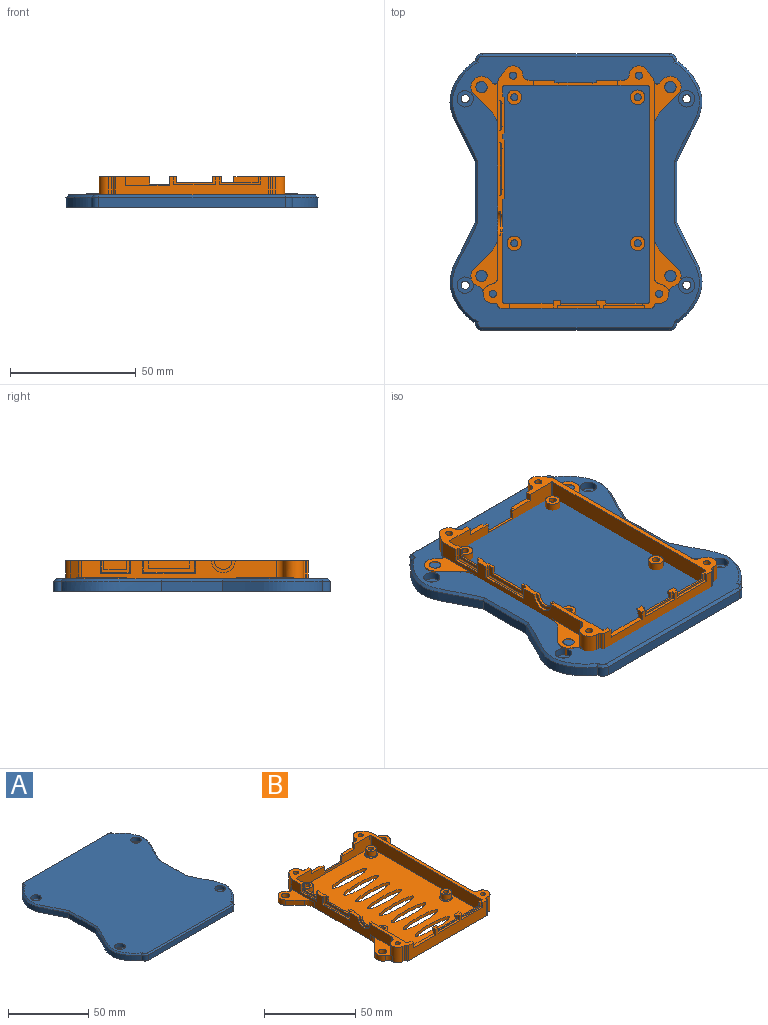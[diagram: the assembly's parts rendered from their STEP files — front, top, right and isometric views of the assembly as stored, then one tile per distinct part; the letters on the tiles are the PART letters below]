
ASSEMBLY  parts=2 mates=1
PART A: 43 faces, bbox 102.5x111.1x6.1 mm
  f0: plane 70.5x2mm, normal (0,1,0), area 141mm2, adj f1,f15,f16,f30
  f1: plane 102x2mm, normal (1,0,0), area 204mm2, adj f0,f2,f16,f30
  f2: plane 70.5x2mm, normal (0,-1,0), area 141mm2, adj f1,f15,f16,f30
  f3: extruded ~40x10.04mm, area 183.4mm2, adj f4,f14,f16,f41
  f4: plane 24x4mm, normal (-1,0,0), area 96mm2, adj f3,f5,f16,f39
  f5: extruded ~40x10.04mm, area 183.4mm2, adj f4,f6,f16,f37
  f6: cylinder r=3mm len=4mm, axis (0,0,1), area 18.8mm2, adj f5,f7,f16,f35
  f7: plane 74x4mm, normal (0,-1,0), area 296mm2, adj f6,f8,f16,f33
  f8: cylinder r=3mm len=4mm, axis (0,0,1), area 18.8mm2, adj f7,f9,f16,f31
  f9: extruded ~40x10.04mm, area 183.4mm2, adj f8,f10,f16,f32
  f10: plane 24x4mm, normal (1,0,0), area 96mm2, adj f9,f11,f16,f34
  f11: extruded ~40x10.04mm, area 183.4mm2, adj f10,f12,f16,f36
  f12: cylinder r=3mm len=4mm, axis (0,0,1), area 18.8mm2, adj f11,f13,f16,f38
  f13: plane 74x4mm, normal (0,1,0), area 296mm2, adj f12,f14,f16,f40
  f14: cylinder r=3mm len=4mm, axis (0,0,1), area 18.8mm2, adj f3,f13,f16,f42
  f15: plane 102x2mm, normal (-1,0,0), area 204mm2, adj f0,f2,f16,f30
  f16: plane 110x101.38mm, normal (0,0,-1), area 2552.6mm2, adj f0,f1,f2,f3,f4,f5,f6,f7
  f17: plane 109.12x99.61mm, normal (0,0,1), area 9261.1mm2, adj f20,f23,f26,f29,f31,f32,f33,f34
  f18: cylinder r=1.65mm len=3.3mm, axis (0,0,1), area 20.7mm2, adj f16,f19
  f19: plane 6.5x6.5mm, normal (0,0,1), area 24.6mm2, adj f18,f20
  f20: cylinder r=3.25mm len=6.5mm, axis (0,0,1), area 61.3mm2, adj f17,f19
  f21: cylinder r=1.65mm len=3.3mm, axis (0,0,1), area 20.7mm2, adj f16,f22
  f22: plane 6.5x6.5mm, normal (0,0,1), area 24.6mm2, adj f21,f23
  f23: cylinder r=3.25mm len=6.5mm, axis (0,0,1), area 61.3mm2, adj f17,f22
  f24: cylinder r=1.65mm len=3.3mm, axis (0,0,1), area 20.7mm2, adj f16,f25
  f25: plane 6.5x6.5mm, normal (0,0,1), area 24.6mm2, adj f24,f26
  f26: cylinder r=3.25mm len=6.5mm, axis (0,0,1), area 61.3mm2, adj f17,f25
  f27: cylinder r=1.65mm len=3.3mm, axis (0,0,1), area 20.7mm2, adj f16,f28
  f28: plane 6.5x6.5mm, normal (0,0,1), area 24.6mm2, adj f27,f29
  f29: cylinder r=3.25mm len=6.5mm, axis (0,0,1), area 61.3mm2, adj f17,f28
  f30: plane 102x70.5mm, normal (0,0,-1), area 7191mm2, adj f0,f1,f2,f15
  f31: cone r=2mm half-angle=45deg, axis (0,0,-1), area 6mm2, adj f8,f17,f32,f33
  f32: bspline ~40.52x11.13mm, area 64.4mm2, adj f9,f17,f31,f34
  f33: plane 74x1mm, normal (0,-0.71,0.71), area 104.7mm2, adj f7,f17,f31,f35
  f34: plane 24.39x1mm, normal (0.71,0,0.71), area 34.2mm2, adj f10,f17,f32,f36
  f35: cone r=2mm half-angle=45deg, axis (0,0,-1), area 6mm2, adj f6,f17,f33,f37
  f36: bspline ~43.19x12.21mm, area 64.4mm2, adj f11,f17,f34,f38
  f37: bspline ~43.19x12.21mm, area 64.4mm2, adj f5,f17,f35,f39
  f38: cone r=2mm half-angle=45deg, axis (0,0,-1), area 6mm2, adj f12,f17,f36,f40
  f39: plane 24.39x1mm, normal (-0.71,0,0.71), area 34.2mm2, adj f4,f17,f37,f41
  f40: plane 74x1mm, normal (0,0.71,0.71), area 104.7mm2, adj f13,f17,f38,f42
  f41: bspline ~40.52x11.13mm, area 64.4mm2, adj f3,f17,f39,f42
  f42: cone r=2mm half-angle=45deg, axis (0,0,-1), area 6mm2, adj f14,f17,f40,f41
PART B: 166 faces, bbox 83.8x96.6x10.6 mm
  f0: plane 96.58x83.83mm, normal (0,0,-1), area 5354.5mm2, adj f1,f6,f7,f8,f9,f37,f38,f39
  f1: cylinder r=2.25mm len=4.5mm, axis (0,0,-1), area 49.5mm2, adj f0,f3
  f2: plane 22.79x10.75mm, normal (0,0,1), area 100.2mm2, adj f8,f9,f89,f119,f120,f121,f122,f123
  f3: plane 22.79x10.75mm, normal (0,0,1), area 100.2mm2, adj f1,f39,f148,f149,f150,f151,f152,f153
  f4: plane 20.07x10.76mm, normal (0,0,1), area 93.7mm2, adj f6,f39,f41,f143,f144,f145,f146,f147
  f5: plane 20.07x10.76mm, normal (0,0,1), area 93.7mm2, adj f7,f89,f124,f125,f126,f127,f128,f129
  f6: cylinder r=2.25mm len=4.5mm, axis (0,0,-1), area 49.5mm2, adj f0,f4
  f7: cylinder r=2.25mm len=4.5mm, axis (0,0,-1), area 49.5mm2, adj f0,f5
  f8: cylinder r=2.25mm len=4.5mm, axis (0,0,-1), area 49.5mm2, adj f0,f2
  f9: cylinder r=3.9mm len=10.3mm, axis (0,0,-1), area 101.4mm2, adj f0,f2,f12,f119,f123,f135
  f10: plane 3x2.8mm, normal (0,0,1), area 7.2mm2, adj f25,f28,f30,f37,f158,f159
  f11: plane 3.5x3mm, normal (0,0,1), area 8.1mm2, adj f29,f32,f35,f37,f159,f160,f163,f165
  f12: plane 30.25x10.45mm, normal (0,0,1), area 99.5mm2, adj f9,f22,f26,f37,f84,f85,f86,f87
  f13: plane 8.65x2.5mm, normal (0,0,1), area 15.1mm2, adj f85,f89,f91,f92,f93,f94,f96,f97
  f14: plane 9.75x2.5mm, normal (0,0,1), area 16.8mm2, adj f85,f86,f87,f88,f89,f94,f97,f103
  f15: plane 15.1x14.15mm, normal (0,0,1), area 78mm2, adj f17,f45,f50,f85,f89,f93,f95,f96
  f16: plane 96.25x20.25mm, normal (0,0,1), area 280.9mm2, adj f23,f24,f26,f34,f35,f36,f37,f38
  f17: cylinder r=1.4mm len=8.3mm, axis (0,0,-1), area 73mm2, adj f15,f20
  f18: plane 2.8x2.8mm, normal (0,0,1), area 6.2mm2, adj f22
  f19: plane 2.8x2.8mm, normal (0,0,1), area 6.2mm2, adj f23
  f20: plane 2.8x2.8mm, normal (0,0,1), area 6.2mm2, adj f17
  f21: plane 2.8x2.8mm, normal (0,0,1), area 6.2mm2, adj f24
  f22: cylinder r=1.4mm len=8.3mm, axis (0,0,-1), area 73mm2, adj f12,f18
  f23: cylinder r=1.4mm len=8.3mm, axis (0,0,1), area 73mm2, adj f16,f19
  f24: cylinder r=1.4mm len=8.3mm, axis (0,0,-1), area 73mm2, adj f16,f21
  f25: plane 3.6x3mm, normal (-1,0,0), area 8.7mm2, adj f10,f26,f27,f30,f37,f157
  f26: plane 57x8.3mm, normal (0,1,0), area 322.8mm2, adj f12,f16,f25,f27,f28,f31,f32,f33
  f27: plane 2.8x2mm, normal (0,0.89,-0.45), area 6.3mm2, adj f25,f26,f28,f30
  f28: plane 2.55x1.8mm, normal (1,0,0), area 3.5mm2, adj f10,f26,f27,f30,f159,f164
  f29: plane 3.5x0.55mm, normal (0,1,0), area 1.9mm2, adj f11,f31,f32,f165
  f30: plane 2.8x0.55mm, normal (0,1,0), area 1.5mm2, adj f10,f25,f27,f28
  f31: plane 3.5x2mm, normal (0,0.89,-0.45), area 7.8mm2, adj f26,f29,f32,f165
  f32: plane 2.55x1.8mm, normal (1,0,0), area 3.5mm2, adj f11,f26,f29,f31,f33,f35
  f33: plane 14.5x0.8mm, normal (0,0,1), area 11.6mm2, adj f26,f32,f34,f35
  f34: plane 2.47x0.8mm, normal (-1,0,0), area 2mm2, adj f16,f26,f33,f35
  f35: plane 16.5x3.17mm, normal (0,-1,0), area 16.5mm2, adj f11,f16,f32,f33,f34,f36,f162,f163
  f36: plane 3.17x1.2mm, normal (-1,0,0), area 3.8mm2, adj f16,f35,f37,f162
  f37: plane 60.4x10.3mm, normal (0,-1,0), area 454.9mm2, adj f0,f10,f11,f12,f16,f25,f36,f38
  f38: cylinder r=0.8mm len=10.3mm, axis (0,0,-1), area 12.9mm2, adj f0,f16,f37,f40
  f39: plane 77.46x10.3mm, normal (1,0,0), area 678.5mm2, adj f0,f3,f4,f16,f41,f147,f148,f153
  f40: plane 10.3x0.18mm, normal (1,0,0), area 1.9mm2, adj f0,f16,f38,f155
  f41: cylinder r=2mm len=10.3mm, axis (0,0,1), area 12.1mm2, adj f0,f4,f16,f39,f42,f143
  f42: plane 10.3x3.48mm, normal (0.82,0.58,0), area 43.8mm2, adj f0,f16,f41,f43
  f43: cylinder r=3.9mm len=10.3mm, axis (0,0,-1), area 99.9mm2, adj f0,f16,f42,f44
  f44: cylinder r=2mm len=10.3mm, axis (0,0,1), area 31.5mm2, adj f0,f16,f43,f45
  f45: plane 38.21x10.3mm, normal (0,1,0), area 205.6mm2, adj f0,f15,f16,f44,f46,f47,f51,f132
  f46: plane 5.3x1mm, normal (-1,0,0), area 5.3mm2, adj f45,f47,f48,f142
  f47: plane 10x2mm, normal (0,0,1), area 18.5mm2, adj f45,f46,f48,f49,f50,f51
  f48: plane 16.5x5.3mm, normal (0,1,0), area 36.1mm2, adj f46,f47,f49,f138,f139,f140,f141,f142
  f49: plane 3.8x1mm, normal (-1,0,0), area 3.8mm2, adj f47,f48,f50,f140
  f50: plane 57x8.3mm, normal (0,-1,0), area 321.3mm2, adj f15,f16,f47,f49,f51,f52,f55,f136
  f51: plane 3x2mm, normal (-1,0,0), area 6mm2, adj f16,f45,f47,f50
  f52: cylinder r=0.5mm len=8.3mm, axis (0,0,1), area 6.5mm2, adj f16,f50,f53,f55
  f53: plane 85.6x8.3mm, normal (-1,0,0), area 710.5mm2, adj f16,f52,f54,f55
  f54: cylinder r=0.5mm len=8.3mm, axis (0,0,1), area 6.5mm2, adj f16,f26,f53,f55
  f55: plane 86.93x58.33mm, normal (0,0,1), area 4061mm2, adj f26,f50,f52,f53,f54,f56,f57,f58
  f56: extruded ~26x5mm, area 109.1mm2, adj f0,f55
  f57: extruded ~26x5mm, area 109.1mm2, adj f0,f55
  f58: extruded ~26x5mm, area 109.1mm2, adj f0,f55
  f59: extruded ~26x5mm, area 109.1mm2, adj f0,f55
  f60: extruded ~26x5mm, area 109.1mm2, adj f0,f55
  f61: extruded ~26x5mm, area 109.1mm2, adj f0,f55
  f62: extruded ~26x5mm, area 109.1mm2, adj f0,f55
  f63: extruded ~26x5mm, area 109.1mm2, adj f0,f55
  f64: cone r=3.15mm half-angle=45deg, axis (0,0,-1), area 14mm2, adj f55,f65
  f65: cylinder r=2.9mm len=5.8mm, axis (0,0,1), area 63.8mm2, adj f64,f67
  f66: plane 5.8x5.8mm, normal (0,0,1), area 20.3mm2, adj f70,f72
  f67: plane 5.8x5.8mm, normal (0,0,1), area 20.3mm2, adj f65,f77
  f68: plane 5.8x5.8mm, normal (0,0,1), area 20.3mm2, adj f79,f80
  f69: plane 5.8x5.8mm, normal (0,0,1), area 20.3mm2, adj f78,f82
  f70: cylinder r=2.9mm len=5.8mm, axis (0,0,1), area 63.8mm2, adj f66,f71
  f71: cone r=3.15mm half-angle=45deg, axis (0,0,-1), area 14mm2, adj f55,f70
  f72: cylinder r=1.4mm len=5mm, axis (0,0,1), area 44mm2, adj f66,f75
  f73: plane 2.8x2.8mm, normal (0,0,1), area 6.2mm2, adj f77
  f74: plane 2.8x2.8mm, normal (0,0,1), area 6.2mm2, adj f78
  f75: plane 2.8x2.8mm, normal (0,0,1), area 6.2mm2, adj f72
  f76: plane 2.8x2.8mm, normal (0,0,1), area 6.2mm2, adj f79
  f77: cylinder r=1.4mm len=5mm, axis (0,0,1), area 44mm2, adj f67,f73
  f78: cylinder r=1.4mm len=5mm, axis (0,0,1), area 44mm2, adj f69,f74
  f79: cylinder r=1.4mm len=5mm, axis (0,0,1), area 44mm2, adj f68,f76
  f80: cylinder r=2.9mm len=5.8mm, axis (0,0,1), area 63.8mm2, adj f68,f81
  f81: cone r=3.15mm half-angle=45deg, axis (0,0,-1), area 14mm2, adj f55,f80
  f82: cylinder r=2.9mm len=5.8mm, axis (0,0,1), area 63.8mm2, adj f69,f83
  f83: cone r=3.15mm half-angle=45deg, axis (0,0,-1), area 14mm2, adj f55,f82
  f84: cylinder r=0.5mm len=8.3mm, axis (0,0,-1), area 6.5mm2, adj f12,f26,f55,f85
  f85: plane 85.6x8.3mm, normal (1,0,0), area 494.1mm2, adj f12,f13,f14,f15,f55,f84,f86,f98
  f86: cylinder r=3.5mm len=7mm, axis (-1,0,0), area 11mm2, adj f12,f14,f85,f87
  f87: plane 9.5x4.75mm, normal (-1,0,0), area 16.2mm2, adj f12,f14,f86,f88
  f88: cylinder r=4.75mm len=9.5mm, axis (-1,0,0), area 14.9mm2, adj f12,f14,f87,f89
  f89: plane 77.46x10.3mm, normal (-1,0,0), area 472.5mm2, adj f0,f2,f5,f12,f13,f14,f15,f88
  f90: plane 10.3x0.18mm, normal (-1,0,0), area 1.9mm2, adj f0,f12,f133,f134
  f91: plane 5.12x1mm, normal (0,-1,0), area 5.1mm2, adj f13,f89,f92,f117
  f92: plane 5.12x0.5mm, normal (-0.71,-0.71,0), area 3.4mm2, adj f13,f91,f94,f118
  f93: plane 11x4.75mm, normal (-1,0,0), area 18.5mm2, adj f13,f15,f95,f101,f102,f109,f112,f113
  f94: plane 20x4.62mm, normal (-1,0,0), area 40.9mm2, adj f13,f14,f92,f103,f104,f105,f115,f118
  f95: plane 3.75x1mm, normal (0,-1,0), area 3.8mm2, adj f15,f93,f96,f102
  f96: plane 14x5.25mm, normal (1,0,0), area 39.8mm2, adj f13,f15,f95,f98,f99,f100,f101,f102
  f97: plane 23x3.62mm, normal (1,0,0), area 31.8mm2, adj f13,f14,f103,f104,f105,f106,f107,f108
  f98: plane 5.75x0.5mm, normal (0.71,0.71,0), area 3.9mm2, adj f15,f85,f96,f99
  f99: plane 15x0.5mm, normal (0.71,0,-0.71), area 10.3mm2, adj f85,f96,f98,f100
  f100: plane 5.75x0.5mm, normal (0.71,-0.71,0), area 3.9mm2, adj f13,f85,f96,f99
  f101: plane 3.75x1mm, normal (0,1,0), area 3.8mm2, adj f13,f93,f96,f102
  f102: plane 9x1mm, normal (0,0,1), area 9mm2, adj f93,f95,f96,f101
  f103: plane 3.12x1mm, normal (0,1,0), area 3.1mm2, adj f14,f94,f97,f104
  f104: plane 16.5x1mm, normal (0,0,1), area 16.5mm2, adj f94,f97,f103,f105
  f105: plane 3.12x1mm, normal (0,-1,0), area 3.1mm2, adj f13,f94,f97,f104
  f106: plane 4.62x0.5mm, normal (0.71,0.71,0), area 2.9mm2, adj f13,f85,f97,f107
  f107: plane 24x1mm, normal (0.89,0,-0.45), area 26.3mm2, adj f85,f97,f106,f108
  f108: plane 4.62x0.5mm, normal (0.71,-0.71,0), area 2.9mm2, adj f14,f85,f97,f107
  f109: plane 5.25x0.5mm, normal (-0.71,0.71,0), area 3.5mm2, adj f13,f93,f110,f112
  f110: plane 5.25x1mm, normal (0,1,0), area 5.2mm2, adj f13,f89,f109,f111
  f111: plane 12x1mm, normal (0,0,1), area 12mm2, adj f89,f110,f112,f114
  f112: plane 12x0.5mm, normal (-0.71,0,0.71), area 8.1mm2, adj f93,f109,f111,f113
  f113: plane 5.25x0.5mm, normal (-0.71,-0.71,0), area 3.5mm2, adj f15,f93,f112,f114
  f114: plane 5.25x1mm, normal (0,-1,0), area 5.2mm2, adj f15,f89,f111,f113
  f115: plane 5.12x0.5mm, normal (-0.71,0.71,0), area 3.4mm2, adj f14,f94,f116,f118
  f116: plane 5.12x1mm, normal (0,1,0), area 5.1mm2, adj f14,f89,f115,f117
  f117: plane 21x1mm, normal (0,0,1), area 21mm2, adj f89,f91,f116,f118
  f118: plane 21x0.5mm, normal (-0.71,0,0.71), area 14.5mm2, adj f92,f94,f115,f117
  f119: cylinder r=3mm len=6.8mm, axis (0,0,-1), area 29.1mm2, adj f2,f9,f12,f89
  f120: cylinder r=8mm len=5.66mm, axis (0,0,-1), area 22mm2, adj f0,f2,f89,f121
  f121: plane 7.16x7.16mm, normal (-0.71,0.71,0), area 35.5mm2, adj f0,f2,f120,f122
  f122: cylinder r=4.25mm len=7.02mm, axis (0,0,-1), area 30mm2, adj f0,f2,f121,f123
  f123: cylinder r=3mm len=3.5mm, axis (0,0,-1), area 13.4mm2, adj f0,f2,f9,f122
  f124: cylinder r=8mm len=5.66mm, axis (0,0,1), area 22mm2, adj f0,f5,f89,f125
  f125: plane 7.16x7.16mm, normal (-0.71,-0.71,0), area 35.5mm2, adj f0,f5,f124,f126
  f126: cylinder r=4.25mm len=7.26mm, axis (0,0,-1), area 46.7mm2, adj f0,f5,f125,f127
  f127: plane 3.5x1.45mm, normal (0.71,0.71,0), area 7.2mm2, adj f0,f5,f126,f128
  f128: cylinder r=1.2mm len=3.5mm, axis (0,0,-1), area 9.6mm2, adj f0,f5,f127,f129
  f129: cylinder r=2mm len=10.3mm, axis (0,0,-1), area 12.1mm2, adj f0,f5,f15,f89,f128,f130
  f130: plane 10.3x3.48mm, normal (-0.82,0.58,0), area 43.8mm2, adj f0,f15,f129,f131
  f131: cylinder r=3.9mm len=10.3mm, axis (0,0,-1), area 99.9mm2, adj f0,f15,f130,f132
  f132: cylinder r=2mm len=10.3mm, axis (0,0,-1), area 31.5mm2, adj f0,f15,f45,f131
  f133: cylinder r=0.8mm len=10.3mm, axis (0,0,1), area 12.9mm2, adj f0,f12,f37,f90
  f134: cylinder r=0.8mm len=10.3mm, axis (0,0,1), area 12.9mm2, adj f0,f12,f90,f135
  f135: plane 10.3x1.2mm, normal (0,-1,0), area 12.4mm2, adj f0,f9,f12,f134
  f136: cylinder r=0.5mm len=8.3mm, axis (0,0,1), area 6.5mm2, adj f15,f50,f55,f85
  f137: plane 3x2mm, normal (1,0,0), area 6mm2, adj f15,f45,f50,f138
  f138: plane 10x2mm, normal (0,0,1), area 18.5mm2, adj f45,f48,f50,f137,f139,f141
  f139: plane 3.8x1mm, normal (1,0,0), area 3.8mm2, adj f48,f50,f138,f140
  f140: plane 13.5x1mm, normal (0,0,1), area 13.5mm2, adj f48,f49,f50,f139
  f141: plane 5.3x1mm, normal (1,0,0), area 5.3mm2, adj f45,f48,f138,f142
  f142: plane 16.5x1mm, normal (0,0,1), area 16.5mm2, adj f45,f46,f48,f141
  f143: cylinder r=1.2mm len=3.5mm, axis (0,0,1), area 9.6mm2, adj f0,f4,f41,f144
  f144: plane 3.5x1.45mm, normal (-0.71,0.71,0), area 7.2mm2, adj f0,f4,f143,f145
  f145: cylinder r=4.25mm len=7.26mm, axis (0,0,-1), area 46.7mm2, adj f0,f4,f144,f146
  f146: plane 7.16x7.16mm, normal (0.71,-0.71,0), area 35.5mm2, adj f0,f4,f145,f147
  f147: cylinder r=8mm len=5.66mm, axis (0,0,-1), area 22mm2, adj f0,f4,f39,f146
  f148: cylinder r=8mm len=5.66mm, axis (0,0,1), area 22mm2, adj f0,f3,f39,f149
  f149: plane 7.16x7.16mm, normal (0.71,0.71,0), area 35.5mm2, adj f0,f3,f148,f150
  f150: cylinder r=4.25mm len=7.02mm, axis (0,0,-1), area 30mm2, adj f0,f3,f149,f151
  f151: cylinder r=3mm len=3.5mm, axis (0,0,1), area 13.4mm2, adj f0,f3,f150,f152
  f152: cylinder r=3.9mm len=10.3mm, axis (0,0,1), area 101.4mm2, adj f0,f3,f16,f151,f153,f154
  f153: cylinder r=3mm len=6.8mm, axis (0,0,1), area 29.1mm2, adj f3,f16,f39,f152
  f154: plane 10.3x1.2mm, normal (0,-1,0), area 12.4mm2, adj f0,f16,f152,f155
  f155: cylinder r=0.8mm len=10.3mm, axis (0,0,-1), area 12.9mm2, adj f0,f16,f40,f154
  f156: plane 3.6x2mm, normal (1,0,0), area 7.2mm2, adj f12,f26,f37,f157
  f157: plane 17.4x2mm, normal (0,0,1), area 34.8mm2, adj f25,f26,f37,f156
  f158: plane 3.17x1.2mm, normal (1,0,0), area 3.8mm2, adj f10,f37,f159,f161
  f159: plane 16.5x3.17mm, normal (0,-1,0), area 16.5mm2, adj f10,f11,f28,f158,f160,f161,f164,f165
  f160: plane 3.17x1.2mm, normal (-1,0,0), area 3.8mm2, adj f11,f37,f159,f161
  f161: plane 16.5x1.2mm, normal (0,0,1), area 19.8mm2, adj f37,f158,f159,f160
  f162: plane 16.5x1.2mm, normal (0,0,1), area 19.8mm2, adj f35,f36,f37,f163
  f163: plane 3.17x1.2mm, normal (1,0,0), area 3.8mm2, adj f11,f35,f37,f162
  f164: plane 14.5x0.8mm, normal (0,0,1), area 11.6mm2, adj f26,f28,f159,f165
  f165: plane 2.55x1.8mm, normal (-1,0,0), area 3.5mm2, adj f11,f26,f29,f31,f159,f164
PLACE A t=(8.57,5.27,48.19)mm
PLACE B t=(-22.43,-44.95,45.19)mm
MATE planar A.f30 <-> B.f0  axis (0,0,-1) through (8.57,5.6,45.19)mm
